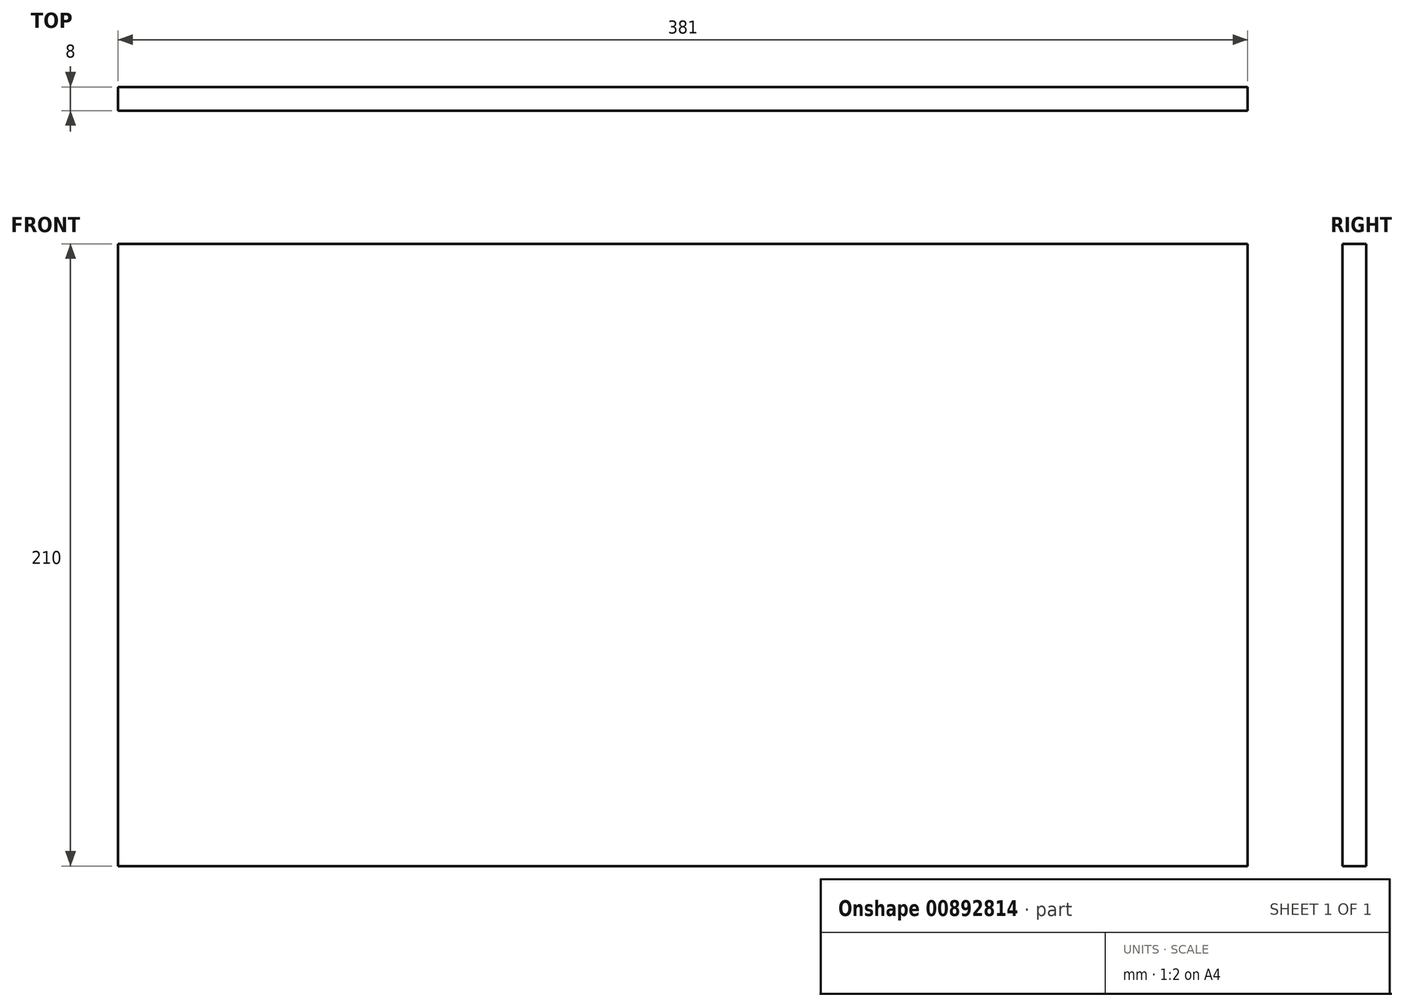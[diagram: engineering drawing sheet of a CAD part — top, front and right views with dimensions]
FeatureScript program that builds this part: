
annotation { "Feature Type Name" : "Feature", "Feature Type Description" : "" }
export const myFeature = defineFeature(function(context is Context, id is Id, definition is map)
    precondition{}
    {
        {
            var Q0;
            Q0=qCreatedBy(makeId("Front.planeOp"),FACE);
            var sketch = newSketch(context, id + "F0", { "sketchPlane" : qUnion([Q0])});
            skLineSegment(sketch, "E0.bottom", {"start": v(-190.5, 105) * mm, "end": v(190.5, 105) * mm});
            skLineSegment(sketch, "E0.top", {"start": v(-190.5, -105) * mm, "end": v(190.5, -105) * mm});
            skLineSegment(sketch, "E0.left", {"start": v(-190.5, 105) * mm, "end": v(-190.5, -105) * mm});
            skLineSegment(sketch, "E0.right", {"start": v(190.5, 105) * mm, "end": v(190.5, -105) * mm});
            skPoint(sketch, "E0.middle", {"position": v(0, 0) * mm});
            skSolve(sketch);
        }
        {
            var Q0;
            Q0=makeQuery(id+"F0.imprint","IMPRINT",FACE,{"disambiguationData":[TD([[makeQuery(id+"F0.imprint","IMPRINT",EDGE,{"derivedFrom":sQuery(id+"F0.wireOp",EDGE,"E0.bottom")}),-1.0]])]});
            extrude(context, id + "F1", {"entities" : qUnion([Q0]), "depth" : 8 * mm, "offsetDistance" : 25 * mm});
        }
    });
